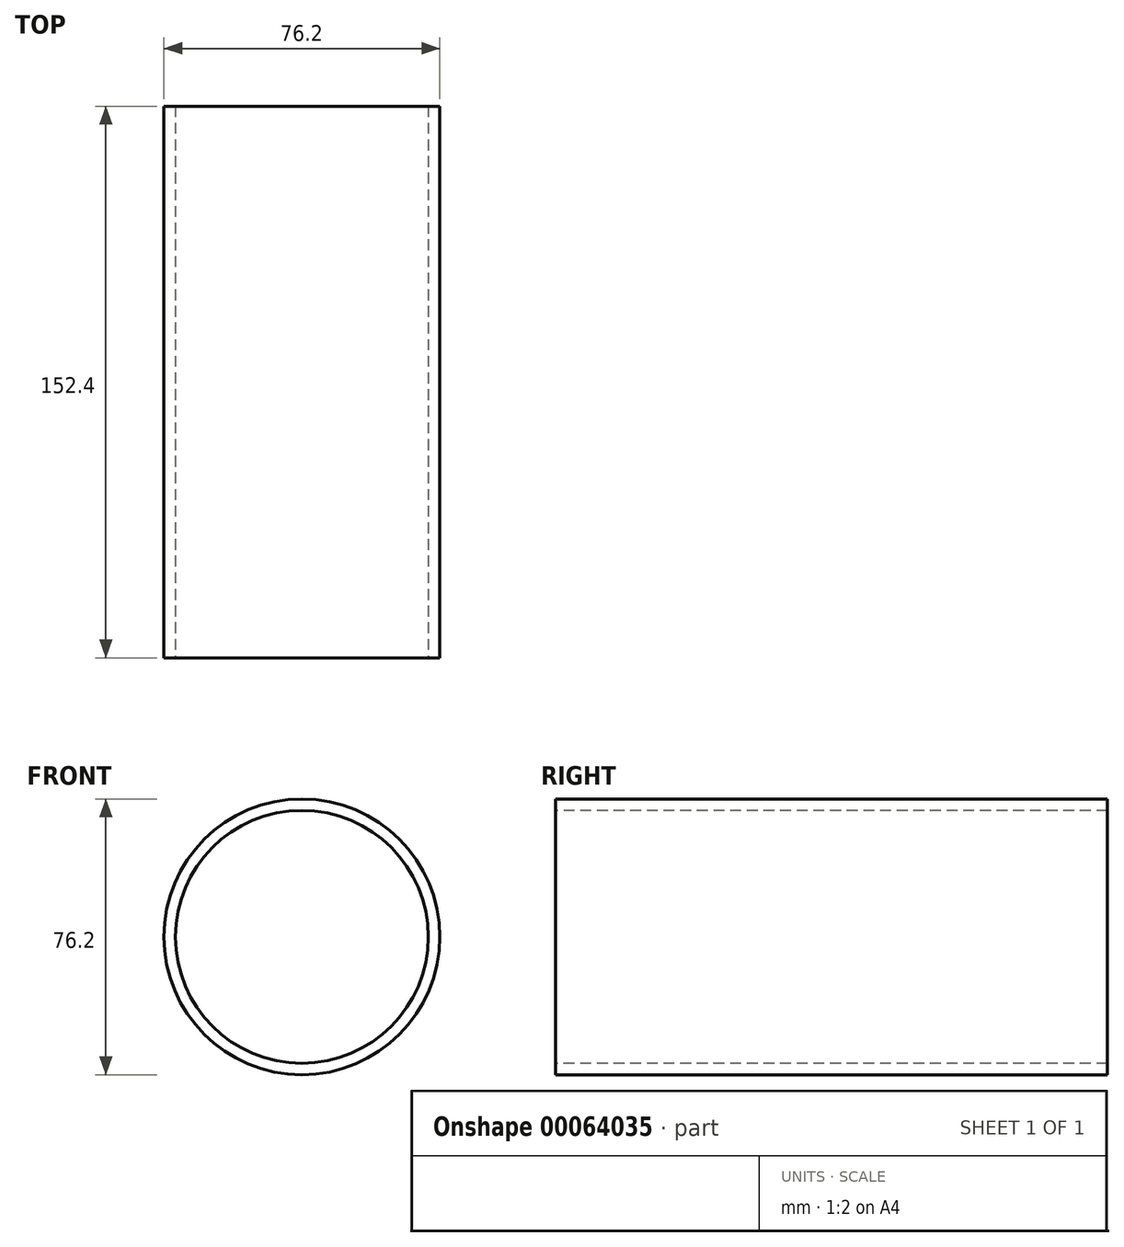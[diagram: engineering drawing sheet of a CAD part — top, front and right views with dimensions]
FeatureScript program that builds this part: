
annotation { "Feature Type Name" : "Feature", "Feature Type Description" : "" }
export const myFeature = defineFeature(function(context is Context, id is Id, definition is map)
    precondition{}
    {
        {
            var Q0;
            Q0=qCreatedBy(makeId("Front.planeOp"),FACE);
            var sketch = newSketch(context, id + "F0", { "sketchPlane" : qUnion([Q0])});
            skCircle(sketch, "E0", {"center": v(0, 0) * mm, "radius": 38.1 * mm});
            skCircle(sketch, "E1", {"center": v(0, 0) * mm, "radius": 34.93 * mm});
            skSolve(sketch);
        }
        {
            var Q0;
            Q0=makeQuery(id+"F0.imprint","IMPRINT",FACE,{"disambiguationData":[TD([[makeQuery(id+"F0.imprint","IMPRINT",EDGE,{"derivedFrom":sQuery(id+"F0.wireOp",EDGE,"E0")}),1.0]])]});
            extrude(context, id + "F1", {"entities" : qUnion([Q0]), "endBound" : BoundingType.SYMMETRIC, "oppositeDirection" : true, "depth" : 152.4 * mm});
        }
        {
            var Q0;
            Q0=qCreatedBy(makeId("Top.planeOp"),FACE);
            cPlane(context, id + "F2", {"entities" : qUnion([Q0]), "cplaneType" : CPlaneType.OFFSET, "offset" : 44.45 * mm, "width" : 152.4 * mm, "height" : 152.4 * mm});
        }
    });
